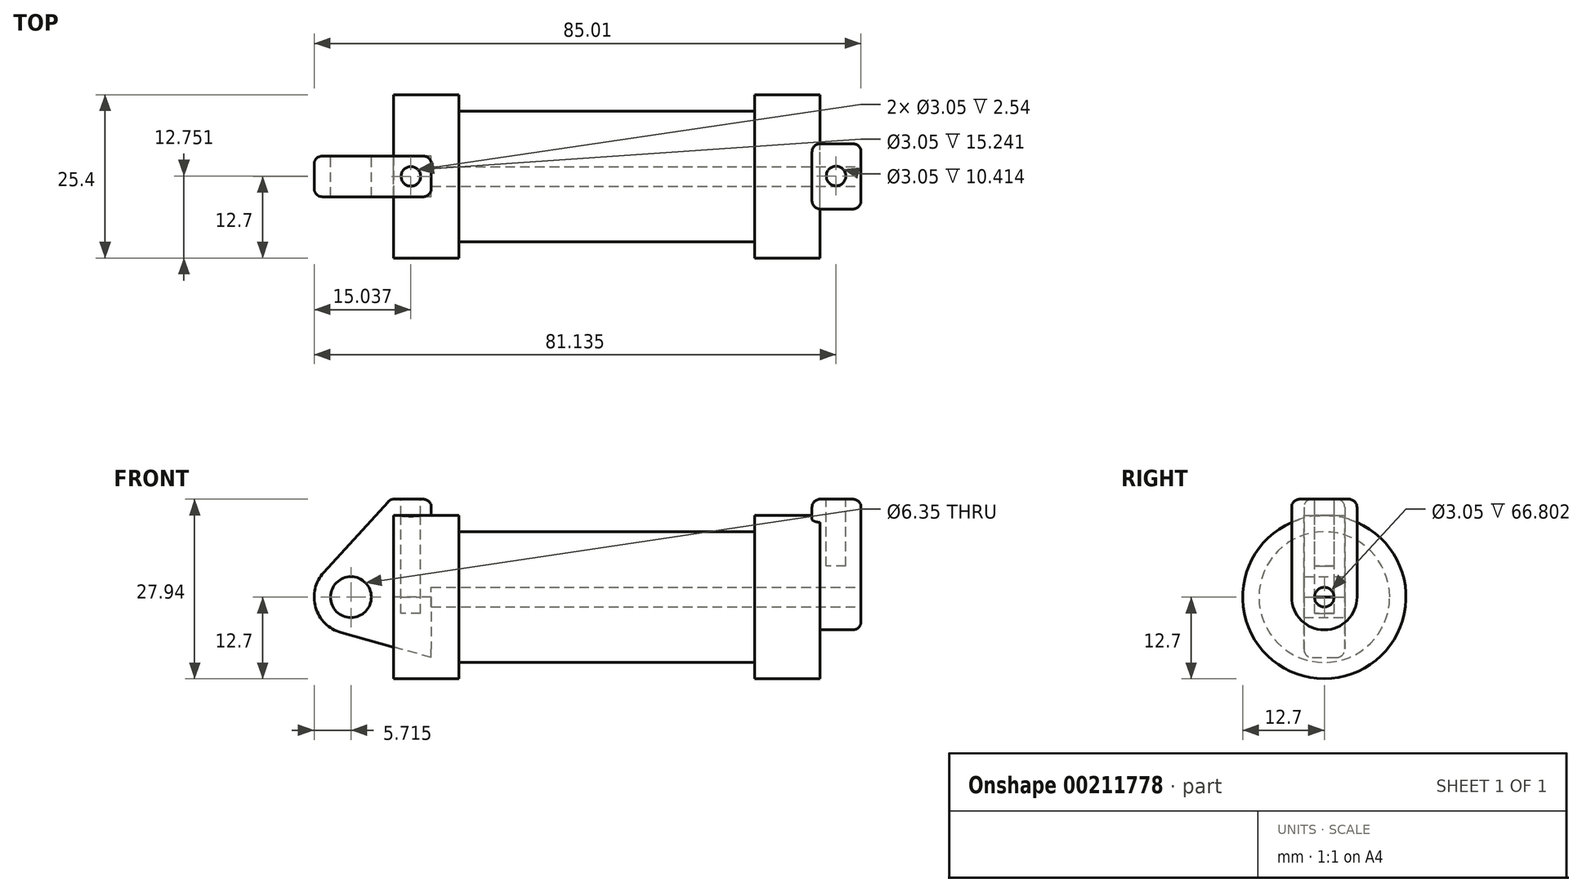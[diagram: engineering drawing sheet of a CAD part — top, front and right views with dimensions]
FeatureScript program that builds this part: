
annotation { "Feature Type Name" : "Feature", "Feature Type Description" : "" }
export const myFeature = defineFeature(function(context is Context, id is Id, definition is map)
    precondition{}
    {
        {
            var Q0;
            Q0=qCreatedBy(makeId("Front.planeOp"),FACE);
            var sketch = newSketch(context, id + "F0", { "sketchPlane" : qUnion([Q0])});
            skLineSegment(sketch, "E0", {"start": v(0, 0) * mm, "end": v(0, 12.7) * mm});
            skLineSegment(sketch, "E1", {"start": v(0, 12.7) * mm, "end": v(10.16, 12.7) * mm});
            skLineSegment(sketch, "E2", {"start": v(10.16, 12.7) * mm, "end": v(10.16, 10.16) * mm});
            skLineSegment(sketch, "E3", {"start": v(10.16, 10.16) * mm, "end": v(56.13, 10.16) * mm});
            skLineSegment(sketch, "E4", {"start": v(56.13, 10.16) * mm, "end": v(56.13, 12.7) * mm});
            skLineSegment(sketch, "E5", {"start": v(56.13, 12.7) * mm, "end": v(66.3, 12.7) * mm});
            skLineSegment(sketch, "E6", {"start": v(66.3, 12.7) * mm, "end": v(66.3, 0) * mm});
            skLineSegment(sketch, "E7", {"start": v(66.3, 0) * mm, "end": v(0, 0) * mm});
            skLineSegment(sketch, "E8", {"start": v(5.84, 15.24) * mm, "end": v(-0.5, 15.24) * mm});
            skLineSegment(sketch, "E9", {"start": v(-0.5, 15.24) * mm, "end": v(-10.88, 3.85) * mm});
            skLineSegment(sketch, "E10", {"start": v(0, 0) * mm, "end": v(-6.65, 0) * mm});
            skCircle(sketch, "E11", {"center": v(-6.65, 0) * mm, "radius": 5.72 * mm});
            skCircle(sketch, "E12", {"center": v(-6.65, 0) * mm, "radius": 3.18 * mm});
            skLineSegment(sketch, "E13", {"start": v(5.84, 15.24) * mm, "end": v(5.84, -9.4) * mm});
            skLineSegment(sketch, "E14", {"start": v(5.84, -9.4) * mm, "end": v(-8.18, -5.5) * mm});
            skSolve(sketch);
        }
        {
            var Q0;
            {var subQ0=sQuery(id+"F0.wireOp",EDGE,"E2");Q0=makeQuery(id+"F0.imprint","IMPRINT",FACE,{"disambiguationData":[TD([[makeQuery(id+"F0.imprint","IMPRINT",EDGE,{"derivedFrom":subQ0}),-1.0]])]});}
            var Q1;
            {var subQ0=sQuery(id+"F0.wireOp",EDGE,"E0");Q1=makeQuery(id+"F0.imprint","IMPRINT",FACE,{"disambiguationData":[TD([[makeQuery(id+"F0.imprint","IMPRINT",EDGE,{"derivedFrom":subQ0}),-1.0]])]});}
            var Q2;
            Q2=sQuery(id+"F0.wireOp",EDGE,"E7");
            revolve(context, id + "F1", {"entities" : qUnion([Q0, Q1]), "axis" : qUnion([Q2]), "revolveType" : RevolveType.FULL});
        }
        {
            var Q0;
            {var subQ3=sQuery(id+"F0.wireOp",EDGE,"E0");Q0=makeQuery(id+"F0.imprint","IMPRINT",FACE,{"disambiguationData":[TD([[makeQuery(id+"F0.imprint","IMPRINT",EDGE,{"derivedFrom":subQ3}),1.0]])]});}
            var Q1;
            {var subQ4=sQuery(id+"F0.wireOp",EDGE,"E12");Q1=makeQuery(id+"F0.imprint","IMPRINT",FACE,{"disambiguationData":[TD([[makeQuery(id+"F0.imprint","IMPRINT",EDGE,{"derivedFrom":subQ4}),-1.0]])]});}
            var Q2;
            {var subQ0=sQuery(id+"F0.wireOp",EDGE,"E14");Q2=makeQuery(id+"F0.imprint","IMPRINT",FACE,{"disambiguationData":[TD([[makeQuery(id+"F0.imprint","IMPRINT",EDGE,{"derivedFrom":subQ0}),-1.0]])]});}
            extrude(context, id + "F2", {"entities" : qUnion([Q0, Q1, Q2]), "endBound" : BoundingType.SYMMETRIC, "depth" : 6.35 * mm});
        }
        {
            var Q0;
            Q0=makeQuery(id+"F1.opRevolve","SWEPT_FACE",FACE,{"disambiguationData":[OSD([sQuery(id+"F0.wireOp",EDGE,"E6")])]});
            var sketch = newSketch(context, id + "F3", { "sketchPlane" : qUnion([Q0])});
            skCircle(sketch, "E15", {"center": v(0, 0) * mm, "radius": 1.52 * mm});
            skCircle(sketch, "E16", {"center": v(0, 0) * mm, "radius": 5.08 * mm});
            skLineSegment(sketch, "E17", {"start": v(-5.08, 0) * mm, "end": v(-5.08, 15.24) * mm});
            skLineSegment(sketch, "E18.bottom", {"start": v(-5.08, 0) * mm, "end": v(5.08, 0) * mm});
            skLineSegment(sketch, "E18.top", {"start": v(-5.08, 15.24) * mm, "end": v(5.08, 15.24) * mm});
            skLineSegment(sketch, "E18.right", {"start": v(5.08, 0) * mm, "end": v(5.08, 15.24) * mm});
            skLineSegment(sketch, "E19.bottom", {"start": v(-5.08, 15.24) * mm, "end": v(-5.08, 15.24) * mm});
            skLineSegment(sketch, "E19.top", {"start": v(-5.08, 0) * mm, "end": v(-5.08, 0) * mm});
            skLineSegment(sketch, "E19.left", {"start": v(-5.08, 15.24) * mm, "end": v(-5.08, 0) * mm});
            skLineSegment(sketch, "E19.right", {"start": v(-5.08, 15.24) * mm, "end": v(-5.08, 0) * mm});
            skSolve(sketch);
        }
        {
            var Q0;
            {var subQ0=sQuery(id+"F3.wireOp",EDGE,"E18.bottom");var subQ1=sQuery(id+"F3.wireOp",EDGE,"E15");var subQ2=makeQuery(id+"F3.imprint","INTERSECT",VERTEX,{"disambiguationData":[OD(0.0)],"derivedFrom":[subQ1,subQ0]});Q0=makeQuery(id+"F3.imprint","IMPRINT",FACE,{"disambiguationData":[TD([[makeQuery(id+"F3.imprint","IMPRINT",EDGE,{"disambiguationData":[TD([[subQ2,-1.0]])],"derivedFrom":subQ1}),1.0]])]});}
            var Q1;
            {var subQ0=sQuery(id+"F3.wireOp",EDGE,"E18.bottom");var subQ1=sQuery(id+"F3.wireOp",EDGE,"E15");var subQ2=makeQuery(id+"F3.imprint","INTERSECT",VERTEX,{"disambiguationData":[OD(0.0)],"derivedFrom":[subQ1,subQ0]});Q1=makeQuery(id+"F3.imprint","IMPRINT",FACE,{"disambiguationData":[TD([[makeQuery(id+"F3.imprint","IMPRINT",EDGE,{"disambiguationData":[TD([[subQ2,1.0]])],"derivedFrom":subQ1}),1.0]])]});}
            var Q2;
            Q2=makeQuery(id+"F1.opRevolve","SWEPT_FACE",FACE,{"disambiguationData":[OSD([sQuery(id+"F0.wireOp",EDGE,"E2")])]});
            extrude(context, id + "F4", {"entities" : qUnion([Q0, Q1]), "operationType" : NewBodyOperationType.REMOVE, "oppositeDirection" : true, "endBoundEntityFace" : qUnion([Q2]), "depth" : 60.45 * mm});
        }
        {
            var Q0;
            Q0=makeQuery(id+"F1.opRevolve","SWEPT_FACE",FACE,{"disambiguationData":[OSD([sQuery(id+"F0.wireOp",EDGE,"E6")])]});
            var sketch = newSketch(context, id + "F5", { "sketchPlane" : qUnion([Q0])});
            skCircle(sketch, "E20", {"center": v(0, 0) * mm, "radius": 1.52 * mm});
            skCircle(sketch, "E21", {"center": v(0, 0) * mm, "radius": 5.08 * mm});
            skLineSegment(sketch, "E22", {"start": v(5.08, 0) * mm, "end": v(5.08, 15.24) * mm});
            skLineSegment(sketch, "E23", {"start": v(-5.08, 0) * mm, "end": v(-5.08, 15.24) * mm});
            skLineSegment(sketch, "E24", {"start": v(-5.08, 15.24) * mm, "end": v(5.08, 15.24) * mm});
            skSolve(sketch);
        }
        {
            var Q0;
            {var subQ0=sQuery(id+"F5.wireOp",EDGE,"E22");var subQ1=sQuery(id+"F5.wireOp",EDGE,"E21");var subQ2=makeQuery(id+"F5.imprint","INTERSECT",VERTEX,{"derivedFrom":[subQ1,subQ0]});Q0=makeQuery(id+"F5.imprint","IMPRINT",FACE,{"disambiguationData":[TD([[makeQuery(id+"F5.imprint","IMPRINT",EDGE,{"disambiguationData":[TD([[subQ2,-1.0]])],"derivedFrom":subQ1}),-1.0]])]});}
            var Q1;
            {var subQ0=sQuery(id+"F5.wireOp",EDGE,"E24");Q1=makeQuery(id+"F5.imprint","IMPRINT",FACE,{"disambiguationData":[TD([[makeQuery(id+"F5.imprint","IMPRINT",EDGE,{"derivedFrom":subQ0}),-1.0]])]});}
            var Q2;
            Q2=makeQuery(id+"F5.imprint","IMPRINT",FACE,{"disambiguationData":[TD([[makeQuery(id+"F5.imprint","IMPRINT",EDGE,{"derivedFrom":sQuery(id+"F5.wireOp",EDGE,"E20")}),-1.0]])]});
            extrude(context, id + "F6", {"entities" : qUnion([Q0, Q1, Q2]), "operationType" : NewBodyOperationType.ADD, "oppositeDirection" : true, "depth" : 1.27 * mm});
        }
        {
            var Q0;
            {var subQ0=sQuery(id+"F5.wireOp",EDGE,"E22");var subQ1=sQuery(id+"F5.wireOp",EDGE,"E21");var subQ2=makeQuery(id+"F5.imprint","INTERSECT",VERTEX,{"derivedFrom":[subQ1,subQ0]});Q0=makeQuery(id+"F5.imprint","IMPRINT",FACE,{"disambiguationData":[TD([[makeQuery(id+"F5.imprint","IMPRINT",EDGE,{"disambiguationData":[TD([[subQ2,-1.0]])],"derivedFrom":subQ1}),-1.0]])]});}
            var Q1;
            {var subQ0=sQuery(id+"F5.wireOp",EDGE,"E24");Q1=makeQuery(id+"F5.imprint","IMPRINT",FACE,{"disambiguationData":[TD([[makeQuery(id+"F5.imprint","IMPRINT",EDGE,{"derivedFrom":subQ0}),-1.0]])]});}
            var Q2;
            Q2=makeQuery(id+"F5.imprint","IMPRINT",FACE,{"disambiguationData":[TD([[makeQuery(id+"F5.imprint","IMPRINT",EDGE,{"derivedFrom":sQuery(id+"F5.wireOp",EDGE,"E20")}),-1.0]])]});
            extrude(context, id + "F7", {"entities" : qUnion([Q0, Q1, Q2]), "operationType" : NewBodyOperationType.ADD, "depth" : 6.35 * mm});
        }
        {
            var Q0;
            {var subQ0=sQuery(id+"F5.wireOp",EDGE,"E24");Q0=makeQuery(id+"F7.boolean.opBoolean","MERGE",FACE,{"derivedFrom":[makeQuery(id+"F6.opExtrude","SWEPT_FACE",FACE,{"disambiguationData":[OSD([subQ0])]}),makeQuery(id+"F7.opExtrude","SWEPT_FACE",FACE,{"disambiguationData":[OSD([subQ0])]})]});}
            var sketch = newSketch(context, id + "F8", { "sketchPlane" : qUnion([Q0])});
            skSolve(sketch);
        }
        {
            var Q0;
            Q0=makeQuery(id+"F2.opExtrude","SWEPT_FACE",FACE,{"disambiguationData":[OSD([sQuery(id+"F0.wireOp",EDGE,"E8")])]});
            var sketch = newSketch(context, id + "F9", { "sketchPlane" : qUnion([Q0])});
            skLineSegment(sketch, "E25", {"start": v(-0.5, 0) * mm, "end": v(1.14, 0) * mm});
            skCircle(sketch, "E26", {"center": v(2.67, 0) * mm, "radius": 1.52 * mm});
            skPoint(sketch, "E27.orphan", {"position": v(2.67, 3.18) * mm});
            skPoint(sketch, "E28.orphan", {"position": v(5.84, 0) * mm});
            skPoint(sketch, "E29.trimOffspring.end.orphan", {"position": v(2.67, -3.18) * mm});
            skSolve(sketch);
        }
        {
            var Q0;
            Q0=makeQuery(id+"F9.imprint","IMPRINT",FACE,{"disambiguationData":[TD([[makeQuery(id+"F9.imprint","IMPRINT",EDGE,{"derivedFrom":sQuery(id+"F9.wireOp",EDGE,"E26")}),1.0]])]});
            extrude(context, id + "F10", {"entities" : qUnion([Q0]), "operationType" : NewBodyOperationType.REMOVE, "oppositeDirection" : true, "depth" : 17.78 * mm});
        }
        {
            var Q0;
            {var subQ0=sQuery(id+"F5.wireOp",EDGE,"E24");Q0=makeQuery(id+"F8.imprint","IMPRINT",FACE,{"disambiguationData":[TD([[makeQuery(id+"F8.imprint","IMPRINT",EDGE,{"derivedFrom":makeQuery(id+"F6.opExtrude","CAP_EDGE",EDGE,{"disambiguationData":[OSD([subQ0])],"isStart":false})}),-1.0]])]});}
            var sketch = newSketch(context, id + "F11", { "sketchPlane" : qUnion([Q0])});
            skCircle(sketch, "E30", {"center": v(68.77, 0.05) * mm, "radius": 1.52 * mm});
            skSolve(sketch);
        }
        {
            var Q0;
            Q0=makeQuery(id+"F11.imprint","IMPRINT",FACE,{"disambiguationData":[TD([[makeQuery(id+"F11.imprint","IMPRINT",EDGE,{"derivedFrom":sQuery(id+"F11.wireOp",EDGE,"E30")}),1.0]])]});
            extrude(context, id + "F12", {"entities" : qUnion([Q0]), "operationType" : NewBodyOperationType.REMOVE, "oppositeDirection" : true, "depth" : 10.4 * mm});
        }
        {
            var Q0;
            Q0=makeQuery(id+"F7.opExtrude","CAP_EDGE",EDGE,{"disambiguationData":[OSD([sQuery(id+"F5.wireOp",EDGE,"E23")])],"isStart":false});
            var Q1;
            {var subQ0=sQuery(id+"F5.wireOp",EDGE,"E24");var subQ1=sQuery(id+"F5.wireOp",EDGE,"E23");Q1=makeQuery(id+"F7.boolean.opBoolean","MERGE",EDGE,{"derivedFrom":[makeQuery(id+"F6.opExtrude","SWEPT_EDGE",EDGE,{"disambiguationData":[OSD([subQ1,subQ0])]}),makeQuery(id+"F7.opExtrude","SWEPT_EDGE",EDGE,{"disambiguationData":[OSD([subQ1,subQ0])]})]});}
            var Q2;
            Q2=makeQuery(id+"F7.opExtrude","CAP_EDGE",EDGE,{"disambiguationData":[OSD([sQuery(id+"F5.wireOp",EDGE,"E24")])],"isStart":false});
            var Q3;
            Q3=makeQuery(id+"F6.opExtrude","CAP_EDGE",EDGE,{"disambiguationData":[OSD([sQuery(id+"F5.wireOp",EDGE,"E24")])],"isStart":false});
            var Q4;
            {var subQ0=sQuery(id+"F5.wireOp",EDGE,"E24");var subQ1=sQuery(id+"F5.wireOp",EDGE,"E22");Q4=makeQuery(id+"F7.boolean.opBoolean","MERGE",EDGE,{"derivedFrom":[makeQuery(id+"F6.opExtrude","SWEPT_EDGE",EDGE,{"disambiguationData":[OSD([subQ1,subQ0])]}),makeQuery(id+"F7.opExtrude","SWEPT_EDGE",EDGE,{"disambiguationData":[OSD([subQ1,subQ0])]})]});}
            var Q5;
            Q5=makeQuery(id+"F6.opExtrude","CAP_EDGE",EDGE,{"disambiguationData":[OSD([sQuery(id+"F5.wireOp",EDGE,"E23")])],"isStart":false});
            var Q6;
            Q6=makeQuery(id+"F6.opExtrude","CAP_EDGE",EDGE,{"disambiguationData":[OSD([sQuery(id+"F5.wireOp",EDGE,"E22")])],"isStart":false});
            fillet(context, id + "F13", {"entities" : qUnion([Q0, Q1, Q2, Q3, Q4, Q5, Q6]), "radius" : 1.27 * mm, "tangentPropagation" : true, "allowEdgeOverflow" : false});
        }
        {
            var Q0;
            Q0=makeQuery(id+"F2.opExtrude","CAP_EDGE",EDGE,{"disambiguationData":[OSD([sQuery(id+"F0.wireOp",EDGE,"E9")])],"isStart":false});
            var Q1;
            Q1=makeQuery(id+"F2.opExtrude","CAP_EDGE",EDGE,{"disambiguationData":[OSD([sQuery(id+"F0.wireOp",EDGE,"E9")])],"isStart":true});
            var Q2;
            Q2=makeQuery(id+"F2.opExtrude","SWEPT_EDGE",EDGE,{"disambiguationData":[OSD([sQuery(id+"F0.wireOp",EDGE,"E8"),sQuery(id+"F0.wireOp",EDGE,"E9")])]});
            var Q3;
            Q3=makeQuery(id+"F2.opExtrude","CAP_EDGE",EDGE,{"disambiguationData":[OSD([sQuery(id+"F0.wireOp",EDGE,"E8")])],"isStart":true});
            var Q4;
            {var subQ0=sQuery(id+"F0.wireOp",EDGE,"E13");Q4=makeQuery(id+"F2.opExtrude","CAP_EDGE",EDGE,{"disambiguationData":[OSD([subQ0]),TDD([makeQuery(id+"F0.imprint","IMPRINT",EDGE,{"disambiguationData":[TD([[makeQuery(id+"F0.imprint","INTERSECT",VERTEX,{"derivedFrom":[sQuery(id+"F0.wireOp",EDGE,"E8"),subQ0]}),-1.0]])],"derivedFrom":subQ0})])],"isStart":true});}
            var Q5;
            Q5=makeQuery(id+"F2.opExtrude","SWEPT_EDGE",EDGE,{"disambiguationData":[OSD([sQuery(id+"F0.wireOp",EDGE,"E8"),sQuery(id+"F0.wireOp",EDGE,"E13")])]});
            var Q6;
            Q6=makeQuery(id+"F2.opExtrude","CAP_EDGE",EDGE,{"disambiguationData":[OSD([sQuery(id+"F0.wireOp",EDGE,"E8")])],"isStart":false});
            var Q7;
            {var subQ0=sQuery(id+"F0.wireOp",EDGE,"E13");Q7=makeQuery(id+"F2.opExtrude","CAP_EDGE",EDGE,{"disambiguationData":[OSD([subQ0]),TDD([makeQuery(id+"F0.imprint","IMPRINT",EDGE,{"disambiguationData":[TD([[makeQuery(id+"F0.imprint","INTERSECT",VERTEX,{"derivedFrom":[sQuery(id+"F0.wireOp",EDGE,"E8"),subQ0]}),-1.0]])],"derivedFrom":subQ0})])],"isStart":false});}
            fillet(context, id + "F14", {"entities" : qUnion([Q0, Q1, Q2, Q3, Q4, Q5, Q6, Q7]), "radius" : 1.27 * mm, "tangentPropagation" : true, "allowEdgeOverflow" : false});
        }
    });
